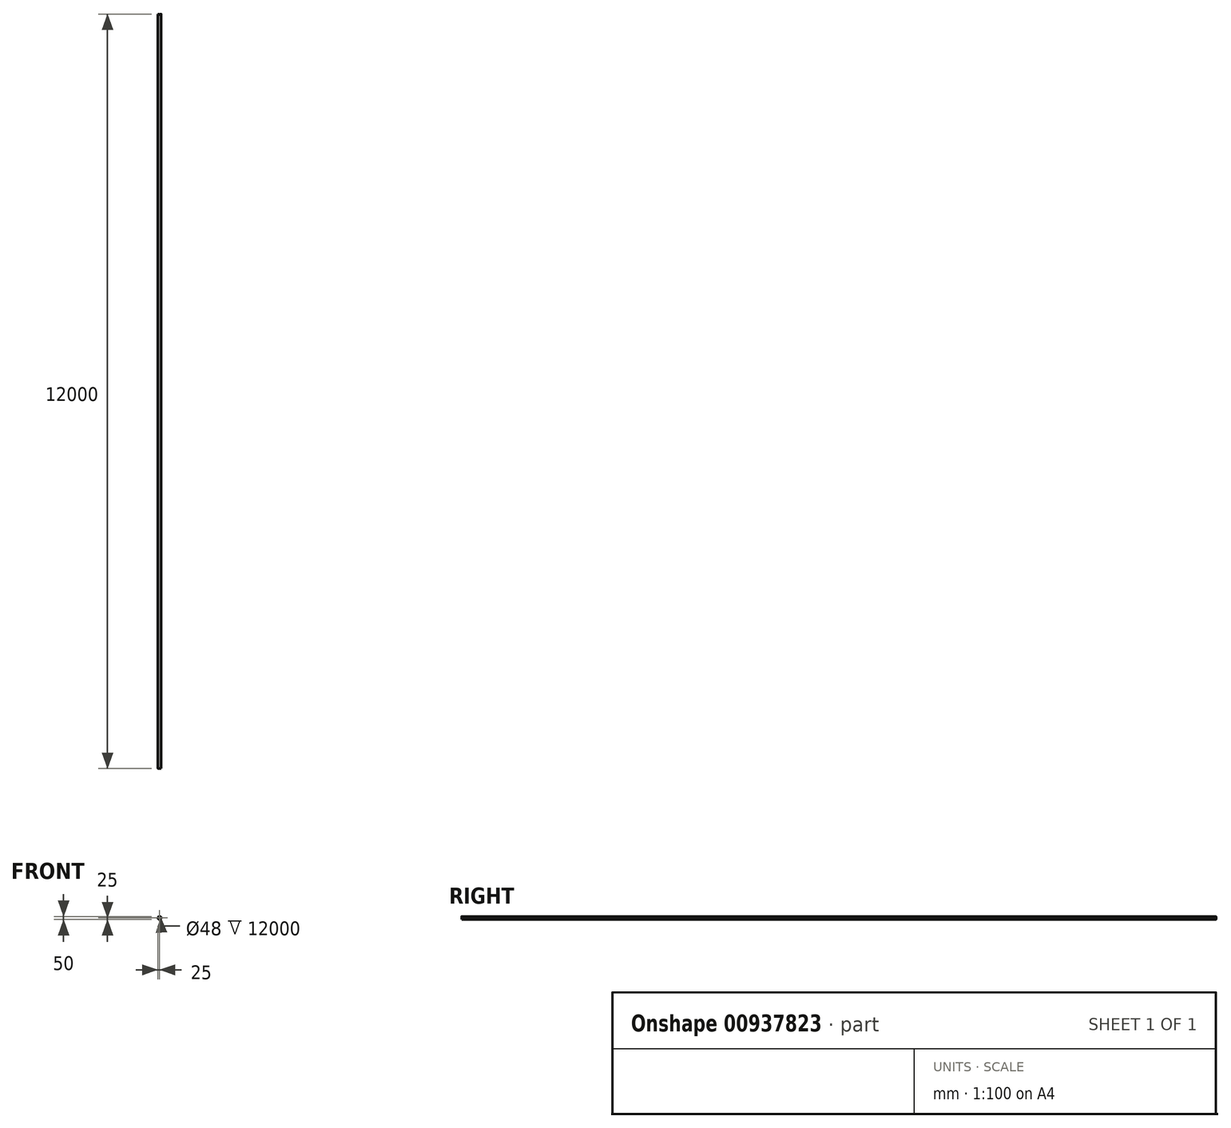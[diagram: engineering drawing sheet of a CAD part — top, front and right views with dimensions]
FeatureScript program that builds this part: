
annotation { "Feature Type Name" : "Feature", "Feature Type Description" : "" }
export const myFeature = defineFeature(function(context is Context, id is Id, definition is map)
    precondition{}
    {
        {
            var Q0;
            Q0=qCreatedBy(makeId("Front.planeOp"),FACE);
            var sketch = newSketch(context, id + "F0", { "sketchPlane" : qUnion([Q0])});
            skCircle(sketch, "E0", {"center": v(0, 0) * mm, "radius": 25 * mm});
            skCircle(sketch, "E1", {"center": v(0, 0) * mm, "radius": 24 * mm});
            skSolve(sketch);
        }
        {
            var Q0;
            Q0=makeQuery(id+"F0.imprint","IMPRINT",FACE,{"disambiguationData":[TD([[makeQuery(id+"F0.imprint","IMPRINT",EDGE,{"derivedFrom":sQuery(id+"F0.wireOp",EDGE,"E0")}),1.0]])]});
            extrude(context, id + "F1", {"entities" : qUnion([Q0]), "depth" : 12000 * mm, "offsetDistance" : 25 * mm});
        }
        {
            var Q0;
            Q0=qCreatedBy(makeId("Top.planeOp"),FACE);
            var sketch = newSketch(context, id + "F2", { "sketchPlane" : qUnion([Q0])});
            skPoint(sketch, "E2", {"position": v(0, 0) * mm});
            skSolve(sketch);
        }
        {
            var Q0;
            Q0=sQuery(id+"F2.wireOp",VERTEX,"E2");
            var Q1;
            Q1=makeQuery(id+"F1.opExtrude","SWEPT_BODY",BODY,{"disambiguationData":[OSD([sQuery(id+"F0.wireOp",EDGE,"E0"),sQuery(id+"F0.wireOp",EDGE,"E1")])]});
            hole(context, id + "F3", {"style" : HoleStyle.SIMPLE, "endStyle" : HoleEndStyle.BLIND, "holeDiameter" : 15 * mm, "majorDiameter" : 5 * mm, "holeDepth" : 25 * mm, "isTappedThrough" : true, "tappedDepth" : 12 * mm, "tapClearance" : 3, "locations" : qUnion([Q0]), "scope" : qUnion([Q1])});
        }
        {
            var Q0;
            Q0=sQuery(id+"F2.wireOp",VERTEX,"E2");
            var Q1;
            Q1=makeQuery(id+"F1.opExtrude","SWEPT_BODY",BODY,{"disambiguationData":[OSD([sQuery(id+"F0.wireOp",EDGE,"E0"),sQuery(id+"F0.wireOp",EDGE,"E1")])]});
            hole(context, id + "F4", {"style" : HoleStyle.SIMPLE, "endStyle" : HoleEndStyle.BLIND, "oppositeDirection" : true, "holeDiameter" : 15 * mm, "majorDiameter" : 5 * mm, "holeDepth" : 25 * mm, "isTappedThrough" : true, "tappedDepth" : 12 * mm, "tapClearance" : 3, "locations" : qUnion([Q0]), "scope" : qUnion([Q1])});
        }
    });
